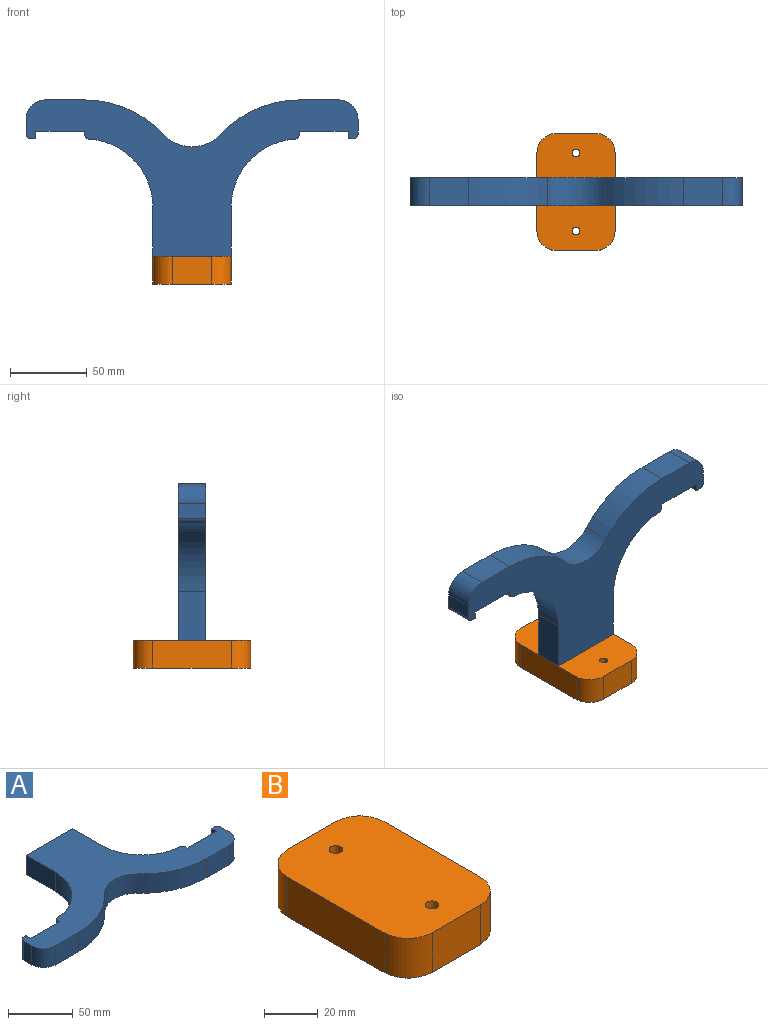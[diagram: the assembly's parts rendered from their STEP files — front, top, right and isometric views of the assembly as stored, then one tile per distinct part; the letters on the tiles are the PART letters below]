
ASSEMBLY  parts=2 mates=1
PART A: 29 faces, bbox 215.9x101.6x18.2 mm
  f0: plane 18.16x9.53mm, normal (-1,0,0), area 173mm2, adj f1,f26,f27,f28
  f1: cylinder r=12.7mm len=18.16mm, axis (0,0,-1), area 362.3mm2, adj f0,f2,f27,f28
  f2: plane 25.4x18.16mm, normal (0,-1,0), area 461.3mm2, adj f1,f3,f27,f28
  f3: cylinder r=69.85mm len=51.22mm, axis (0,0,-1), area 1044.3mm2, adj f2,f4,f27,f28
  f4: cylinder r=25.4mm len=37.25mm, axis (0,0,-1), area 759.5mm2, adj f3,f5,f27,f28
  f5: cylinder r=69.85mm len=51.22mm, axis (0,0,-1), area 1044.3mm2, adj f4,f6,f27,f28
  f6: plane 25.4x18.16mm, normal (0,-1,0), area 461.3mm2, adj f5,f7,f27,f28
  f7: cylinder r=12.7mm len=18.16mm, axis (0,0,-1), area 362.3mm2, adj f6,f8,f27,f28
  f8: plane 18.16x9.53mm, normal (1,0,0), area 173mm2, adj f7,f9,f27,f28
  f9: cylinder r=3.17mm len=18.16mm, axis (0,0,-1), area 90.6mm2, adj f8,f10,f27,f28
  f10: plane 18.16x3.18mm, normal (0,1,0), area 57.7mm2, adj f9,f11,f27,f28
  f11: plane 18.16x5.08mm, normal (-1,0,0), area 92.3mm2, adj f10,f12,f27,f28
  f12: plane 31.75x18.16mm, normal (0,1,0), area 576.6mm2, adj f11,f13,f27,f28
  f13: plane 18.16x2.01mm, normal (1,0,0), area 36.5mm2, adj f12,f14,f27,f28
  f14: cylinder r=3.17mm len=18.16mm, axis (0,0,-1), area 86.7mm2, adj f13,f15,f27,f28
  f15: cylinder r=44.45mm len=44.35mm, axis (0,0,-1), area 1214.2mm2, adj f14,f16,f27,f28
  f16: plane 31.75x18.16mm, normal (1,0,0), area 576.6mm2, adj f15,f17,f27,f28
  f17: plane 50.8x18.16mm, normal (0,1,0), area 922.6mm2, adj f16,f18,f27,f28
  f18: plane 31.75x18.16mm, normal (-1,0,0), area 576.6mm2, adj f17,f19,f27,f28
  f19: cylinder r=44.45mm len=44.35mm, axis (0,0,-1), area 1214.2mm2, adj f18,f20,f27,f28
  f20: cylinder r=3.17mm len=18.16mm, axis (0,0,-1), area 86.7mm2, adj f19,f21,f27,f28
  f21: plane 18.16x2.01mm, normal (-1,0,0), area 36.5mm2, adj f20,f22,f27,f28
  f22: plane 31.75x18.16mm, normal (0,1,0), area 576.6mm2, adj f21,f23,f27,f28
  f23: plane 18.16x4.6mm, normal (1,0,0), area 83.5mm2, adj f22,f24,f27,f28
  f24: cylinder r=0.48mm len=18.16mm, axis (0,0,-1), area 13.7mm2, adj f23,f25,f27,f28
  f25: plane 18.16x2.69mm, normal (0,1,0), area 48.9mm2, adj f24,f26,f27,f28
  f26: cylinder r=3.17mm len=18.16mm, axis (0,0,-1), area 90.6mm2, adj f0,f25,f27,f28
  f27: plane 215.9x101.6mm, normal (0,0,1), area 8053.4mm2, adj f0,f1,f2,f3,f4,f5,f6,f7
  f28: plane 215.9x101.6mm, normal (0,0,-1), area 8053.4mm2, adj f0,f1,f2,f3,f4,f5,f6,f7
PART B: 12 faces, bbox 50.8x76.2x18.2 mm
  f0: plane 50.8x18.16mm, normal (1,0,0), area 922.6mm2, adj f1,f9,f10,f11
  f1: cylinder r=12.7mm len=18.16mm, axis (0,0,-1), area 362.3mm2, adj f0,f2,f10,f11
  f2: plane 25.4x18.16mm, normal (0,1,0), area 461.3mm2, adj f1,f3,f10,f11
  f3: cylinder r=12.7mm len=18.16mm, axis (0,0,-1), area 362.3mm2, adj f2,f4,f10,f11
  f4: plane 50.8x18.16mm, normal (-1,0,0), area 922.6mm2, adj f3,f5,f10,f11
  f5: cylinder r=12.7mm len=18.16mm, axis (0,0,-1), area 362.3mm2, adj f4,f6,f10,f11
  f6: plane 25.4x18.16mm, normal (0,-1,0), area 461.3mm2, adj f5,f9,f10,f11
  f7: cylinder r=2.54mm len=18.16mm, axis (0,0,-1), area 289.8mm2, adj f10,f11
  f8: cylinder r=2.54mm len=18.16mm, axis (0,0,-1), area 289.8mm2, adj f10,f11
  f9: cylinder r=12.7mm len=18.16mm, axis (0,0,-1), area 362.3mm2, adj f0,f6,f10,f11
  f10: plane 76.2x50.8mm, normal (0,0,1), area 3692mm2, adj f0,f1,f2,f3,f4,f5,f6,f7
  f11: plane 76.2x50.8mm, normal (0,0,-1), area 3692mm2, adj f0,f1,f2,f3,f4,f5,f6,f7
PLACE A rot(axis=(-1,0,0),90deg) t=(-0.4,-5.39,116.6)mm
PLACE B t=(-0.4,3.69,-3.16)mm
MATE fastened A.f17 <-> B.f10  axis (0,0,-1) through (-0.4,3.69,15)mm
